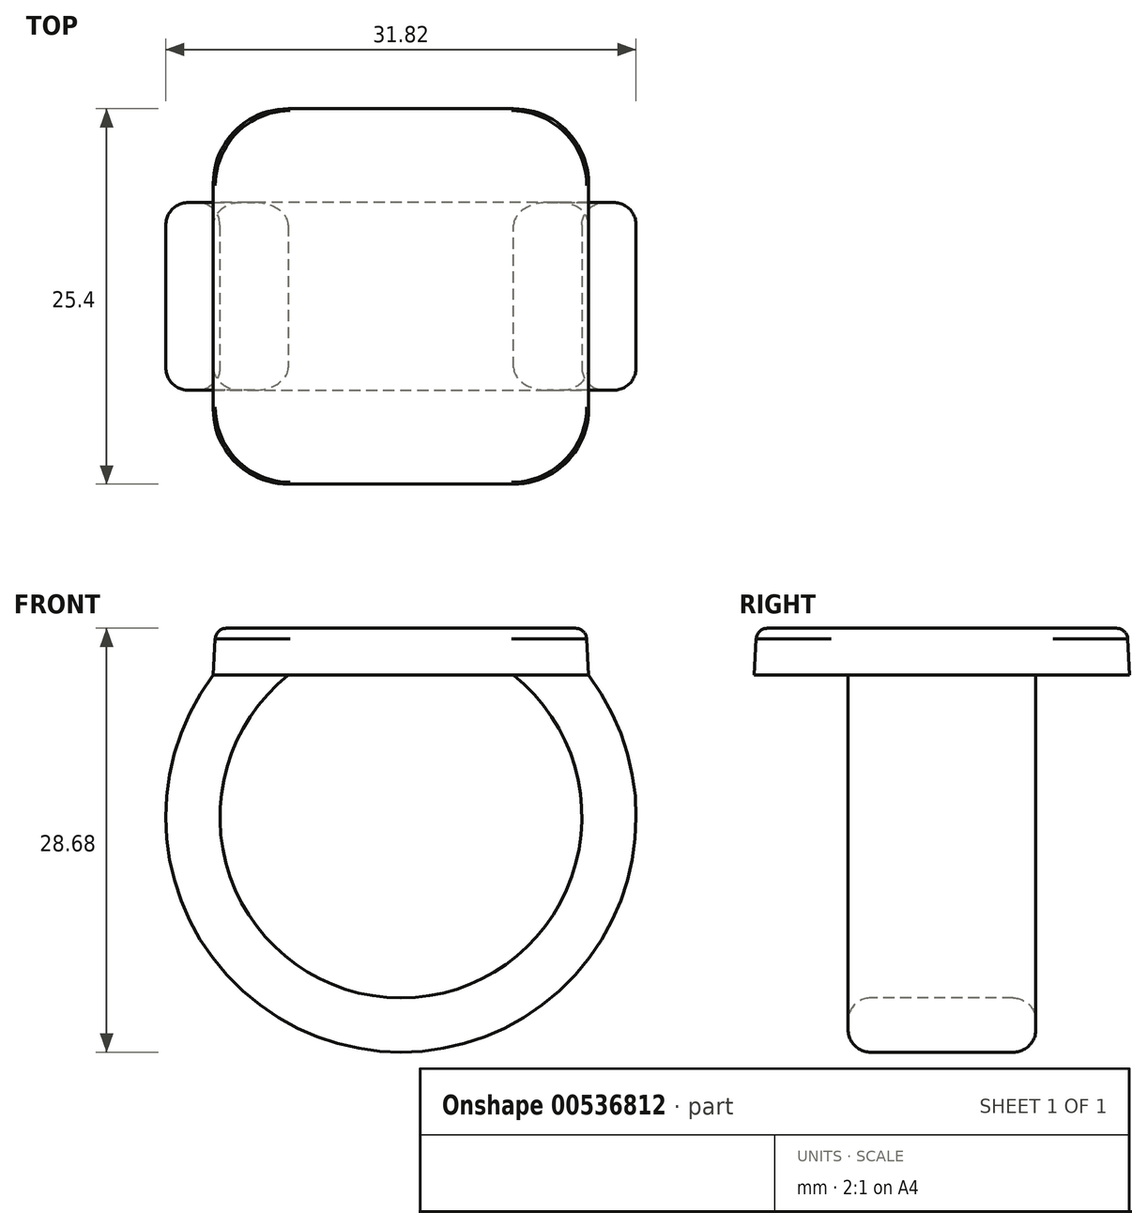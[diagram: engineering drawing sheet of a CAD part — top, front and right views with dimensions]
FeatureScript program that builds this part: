
annotation { "Feature Type Name" : "Feature", "Feature Type Description" : "" }
export const myFeature = defineFeature(function(context is Context, id is Id, definition is map)
    precondition{}
    {
        {
            var Q0;
            Q0=qCreatedBy(makeId("Top.planeOp"),FACE);
            var sketch = newSketch(context, id + "F0", { "sketchPlane" : qUnion([Q0])});
            skLineSegment(sketch, "E0.bottom", {"start": v(12.7, 12.7) * mm, "end": v(-12.7, 12.7) * mm});
            skLineSegment(sketch, "E0.top", {"start": v(12.7, -12.7) * mm, "end": v(-12.7, -12.7) * mm});
            skLineSegment(sketch, "E0.left", {"start": v(12.7, 12.7) * mm, "end": v(12.7, -12.7) * mm});
            skLineSegment(sketch, "E0.right", {"start": v(-12.7, 12.7) * mm, "end": v(-12.7, -12.7) * mm});
            skPoint(sketch, "E0.middle", {"position": v(0, 0) * mm});
            skSolve(sketch);
        }
        {
            var Q0;
            Q0 = qSketchRegion(id + "F0", true);
            extrude(context, id + "F1", {"entities" : qUnion([Q0]), "depth" : 3.17 * mm, "offsetDistance" : 25.4 * mm, "hasDraft" : true, "draftAngle" : 3 * degree, "draftPullDirection" : true});
        }
        {
            var Q0;
            Q0=qCreatedBy(makeId("Front.planeOp"),FACE);
            var sketch = newSketch(context, id + "F2", { "sketchPlane" : qUnion([Q0])});
            skArc(sketch, "E1", {"start": v(-10.16, 0) * mm, "mid": v(0, -23.56) * mm, "end": v(10.16, 0) * mm});
            skSolve(sketch);
        }
        {
            var Q0;
            Q0=makeQuery(id+"F1.opExtrude","CAP_FACE",FACE,{"disambiguationData":[OSD([sQuery(id+"F0.wireOp",EDGE,"E0.bottom"),sQuery(id+"F0.wireOp",EDGE,"E0.top"),sQuery(id+"F0.wireOp",EDGE,"E0.left"),sQuery(id+"F0.wireOp",EDGE,"E0.right")])],"isStart":true});
            var sketch = newSketch(context, id + "F3", { "sketchPlane" : qUnion([Q0])});
            skLineSegment(sketch, "E2.bottom", {"start": v(-7.62, -6.35) * mm, "end": v(-12.7, -6.35) * mm});
            skLineSegment(sketch, "E2.top", {"start": v(-7.62, 6.35) * mm, "end": v(-12.7, 6.35) * mm});
            skLineSegment(sketch, "E2.left", {"start": v(-7.62, -6.35) * mm, "end": v(-7.62, 6.35) * mm});
            skLineSegment(sketch, "E2.right", {"start": v(-12.7, -6.35) * mm, "end": v(-12.7, 6.35) * mm});
            skPoint(sketch, "E2.middle", {"position": v(-10.16, 0) * mm});
            skSolve(sketch);
        }
        {
            var Q0;
            Q0 = qSketchRegion(id + "F3", true);
            var Q1;
            Q1 = qConstructionFilter(qBodyType(qCreatedBy(id + "F2" ,EDGE), BodyType.WIRE), ConstructionObject.NO);
            sweep(context, id + "F4", {"operationType" : NewBodyOperationType.ADD, "profiles" : qUnion([Q0]), "path" : qUnion([Q1])});
        }
        {
            var Q0;
            Q0=qCreatedBy(makeId("Front.planeOp"),FACE);
            var sketch = newSketch(context, id + "F5", { "sketchPlane" : qUnion([Q0])});
            skLineSegment(sketch, "E3.0", {"start": v(10.16, 0) * mm, "end": v(7.62, 0) * mm});
            skLineSegment(sketch, "E3.1", {"start": v(10.01, -2.54) * mm, "end": v(10.16, 0) * mm});
            skArc(sketch, "E3.2", {"start": v(10.01, -2.54) * mm, "mid": v(8.9, -1.18) * mm, "end": v(7.62, 0) * mm});
            skPoint(sketch, "E4.orphan", {"position": v(12.7, 0) * mm});
            skPoint(sketch, "E5.trimOffspring.end.orphan", {"position": v(-12.7, 0) * mm});
            skPoint(sketch, "E5.trimOffspring.start.orphan", {"position": v(-7.62, 0) * mm});
            skSolve(sketch);
        }
        {
            var Q0;
            Q0 = qSketchRegion(id + "F5", true);
            var Q1;
            Q1=makeQuery(id+"F4.opSweep","SWEPT_FACE",FACE,{"disambiguationData":[OSD([sQuery(id+"F2.wireOp",EDGE,"E1"),sQuery(id+"F3.wireOp",EDGE,"E2.top")])]});
            var Q2;
            Q2=makeQuery(id+"F4.opSweep","SWEPT_FACE",FACE,{"disambiguationData":[OSD([sQuery(id+"F2.wireOp",EDGE,"E1"),sQuery(id+"F3.wireOp",EDGE,"E2.bottom")])]});
            extrude(context, id + "F6", {"entities" : qUnion([Q0]), "operationType" : NewBodyOperationType.ADD, "endBound" : BoundingType.UP_TO_SURFACE, "depth" : 25.4 * mm, "endBoundEntityFace" : qUnion([Q1]), "offsetDistance" : 25.4 * mm, "hasSecondDirection" : true, "secondDirectionBound" : SecondDirectionBoundingType.UP_TO_SURFACE, "secondDirectionOppositeDirection" : true, "secondDirectionDepth" : 25.4 * mm, "secondDirectionBoundEntityFace" : qUnion([Q2])});
        }
        {
            var Q0;
            Q0=makeQuery(id+"F1.opExtrude","SWEPT_EDGE",EDGE,{"disambiguationData":[OSD([sQuery(id+"F0.wireOp",EDGE,"E0.bottom"),sQuery(id+"F0.wireOp",EDGE,"E0.right")])]});
            var Q1;
            Q1=makeQuery(id+"F1.opExtrude","SWEPT_EDGE",EDGE,{"disambiguationData":[OSD([sQuery(id+"F0.wireOp",EDGE,"E0.bottom"),sQuery(id+"F0.wireOp",EDGE,"E0.left")])]});
            var Q2;
            Q2=makeQuery(id+"F1.opExtrude","SWEPT_EDGE",EDGE,{"disambiguationData":[OSD([sQuery(id+"F0.wireOp",EDGE,"E0.top"),sQuery(id+"F0.wireOp",EDGE,"E0.left")])]});
            var Q3;
            Q3=makeQuery(id+"F1.opExtrude","SWEPT_EDGE",EDGE,{"disambiguationData":[OSD([sQuery(id+"F0.wireOp",EDGE,"E0.top"),sQuery(id+"F0.wireOp",EDGE,"E0.right")])]});
            fillet(context, id + "F7", {"entities" : qUnion([Q0, Q1, Q2, Q3]), "radius" : 5.08 * mm, "tangentPropagation" : true, "allowEdgeOverflow" : false});
        }
        {
            var Q0;
            {var subQ0=sQuery(id+"F3.wireOp",EDGE,"E2.top");var subQ1=sQuery(id+"F2.wireOp",EDGE,"E1");Q0=makeQuery(id+"F6.boolean.opBoolean","MERGE",EDGE,{"derivedFrom":[makeQuery(id+"F4.opSweep","SWEPT_EDGE",EDGE,{"disambiguationData":[OSD([subQ1,subQ0,sQuery(id+"F3.wireOp",EDGE,"E2.left")])]}),makeQuery(id+"F6.opExtrude","TWEAK_EDGE",EDGE,{"derivedFrom":[makeQuery(id+"F4.opSweep","SWEPT_FACE",FACE,{"disambiguationData":[OSD([subQ1,subQ0])]}),makeQuery(id+"F5.imprint","IMPRINT",EDGE,{"derivedFrom":sQuery(id+"F5.wireOp",EDGE,"E3.2")})]})]});}
            var Q1;
            Q1=makeQuery(id+"F4.opSweep","SWEPT_EDGE",EDGE,{"disambiguationData":[OSD([sQuery(id+"F0.wireOp",EDGE,"E0.right"),sQuery(id+"F2.wireOp",EDGE,"E1"),sQuery(id+"F3.wireOp",EDGE,"E2.top"),sQuery(id+"F3.wireOp",EDGE,"E2.right")])]});
            var Q2;
            Q2=makeQuery(id+"F4.opSweep","SWEPT_EDGE",EDGE,{"disambiguationData":[OSD([sQuery(id+"F0.wireOp",EDGE,"E0.right"),sQuery(id+"F2.wireOp",EDGE,"E1"),sQuery(id+"F3.wireOp",EDGE,"E2.bottom"),sQuery(id+"F3.wireOp",EDGE,"E2.right")])]});
            var Q3;
            {var subQ0=sQuery(id+"F3.wireOp",EDGE,"E2.bottom");var subQ1=sQuery(id+"F2.wireOp",EDGE,"E1");Q3=makeQuery(id+"F6.boolean.opBoolean","MERGE",EDGE,{"derivedFrom":[makeQuery(id+"F4.opSweep","SWEPT_EDGE",EDGE,{"disambiguationData":[OSD([subQ1,subQ0,sQuery(id+"F3.wireOp",EDGE,"E2.left")])]}),makeQuery(id+"F6.opExtrude","TWEAK_EDGE",EDGE,{"derivedFrom":[makeQuery(id+"F4.opSweep","SWEPT_FACE",FACE,{"disambiguationData":[OSD([subQ1,subQ0])]}),makeQuery(id+"F5.imprint","IMPRINT",EDGE,{"derivedFrom":sQuery(id+"F5.wireOp",EDGE,"E3.2")})]})]});}
            fillet(context, id + "F8", {"entities" : qUnion([Q0, Q1, Q2, Q3]), "radius" : 1.52 * mm, "tangentPropagation" : true, "allowEdgeOverflow" : false});
        }
        {
            var Q0;
            Q0=makeQuery(id+"F1.opExtrude","CAP_FACE",FACE,{"disambiguationData":[OSD([sQuery(id+"F0.wireOp",EDGE,"E0.bottom"),sQuery(id+"F0.wireOp",EDGE,"E0.top"),sQuery(id+"F0.wireOp",EDGE,"E0.left"),sQuery(id+"F0.wireOp",EDGE,"E0.right")])],"isStart":false});
            fillet(context, id + "F9", {"entities" : qUnion([Q0]), "radius" : 0.76 * mm, "tangentPropagation" : true, "allowEdgeOverflow" : false});
        }
    });
